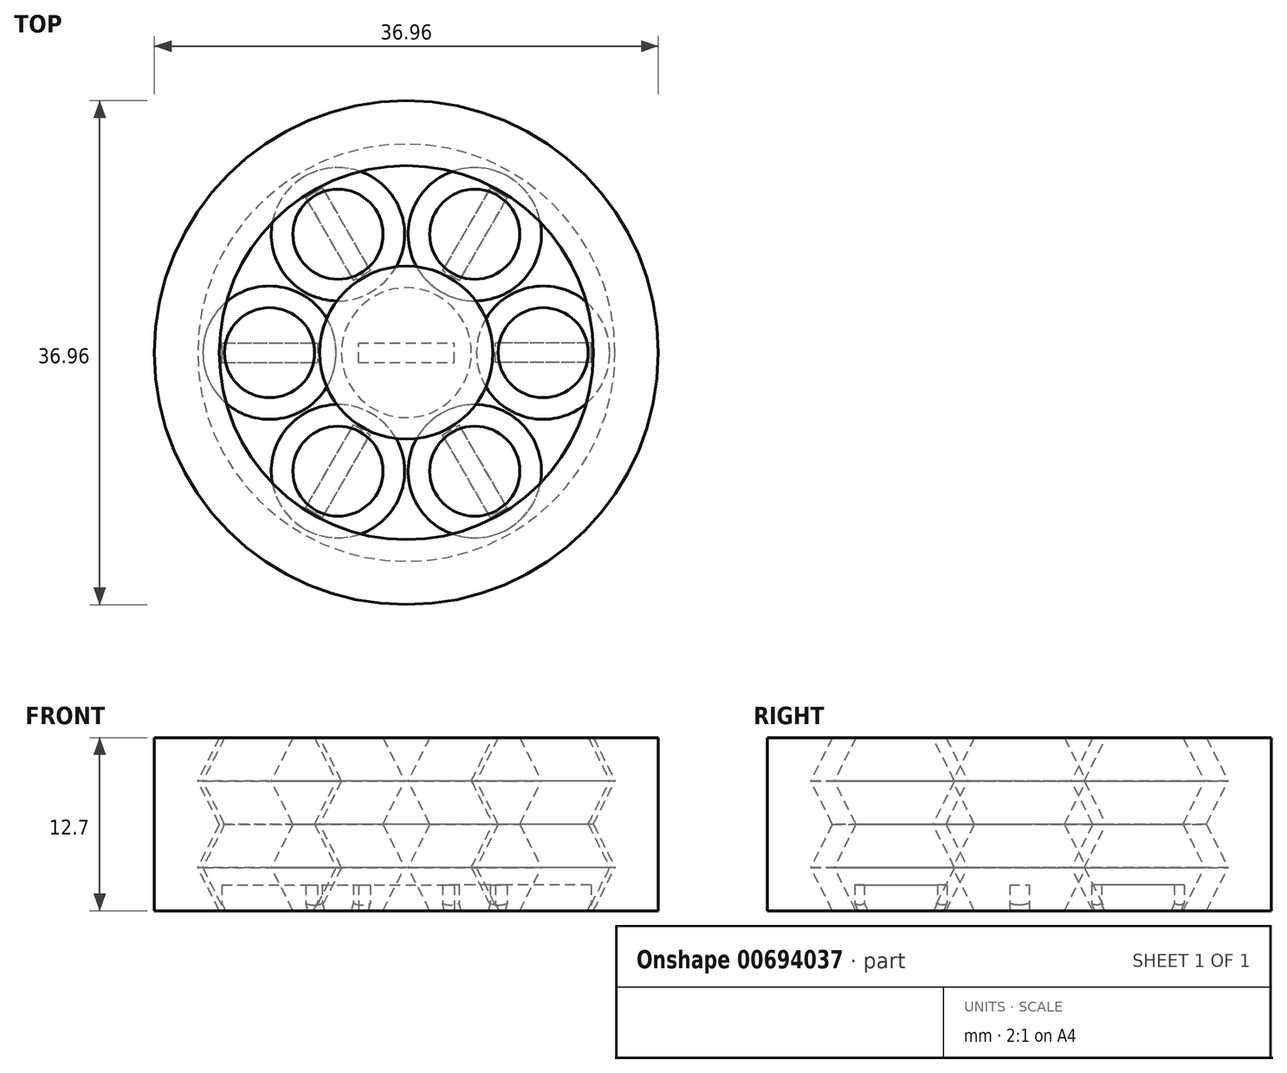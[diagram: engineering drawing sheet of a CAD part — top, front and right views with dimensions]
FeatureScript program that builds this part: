
annotation { "Feature Type Name" : "Feature", "Feature Type Description" : "" }
export const myFeature = defineFeature(function(context is Context, id is Id, definition is map)
    precondition{}
    {
        {
            var Q0;
            Q0=qCreatedBy(makeId("Front.planeOp"),FACE);
            var sketch = newSketch(context, id + "F0", { "sketchPlane" : qUnion([Q0])});
            skLineSegment(sketch, "E0", {"start": v(0, 0) * mm, "end": v(3.17, 0) * mm});
            skLineSegment(sketch, "E1", {"start": v(3.17, 12.7) * mm, "end": v(0, 12.7) * mm});
            skLineSegment(sketch, "E2", {"start": v(6.35, 0) * mm, "end": v(6.86, 0) * mm});
            skLineSegment(sketch, "E3", {"start": v(6.86, 12.7) * mm, "end": v(10.03, 12.7) * mm});
            skLineSegment(sketch, "E4", {"start": v(8.45, 12.7) * mm, "end": v(8.45, 0) * mm});
            skLineSegment(sketch, "E5", {"start": v(8.45, 0) * mm, "end": v(6.86, 0) * mm});
            skLineSegment(sketch, "E6.MirrorCS", {"start": v(12.38, 3.68) * mm, "end": v(12.54, 3.68) * mm});
            skLineSegment(sketch, "E7.MirrorCS", {"start": v(8.45, 0) * mm, "end": v(10.03, 0) * mm});
            skLineSegment(sketch, "E8.MirrorCS", {"start": v(16.9, 0) * mm, "end": v(13.72, 0) * mm});
            skLineSegment(sketch, "E9.MirrorCS", {"start": v(13.72, 12.7) * mm, "end": v(16.9, 12.7) * mm});
            skLineSegment(sketch, "E10.MirrorCS", {"start": v(16.9, 12.7) * mm, "end": v(16.9, 0) * mm});
            skPoint(sketch, "E11.orphan", {"position": v(6.35, 3.18) * mm});
            skPoint(sketch, "E12.start.orphan", {"position": v(6.35, 9.53) * mm});
            skPoint(sketch, "E13.orphan", {"position": v(6.35, 12.7) * mm});
            skPoint(sketch, "E14.orphan", {"position": v(10.54, 9.53) * mm});
            skPoint(sketch, "E15.MirrorCS.end.orphan", {"position": v(10.54, 12.7) * mm});
            skPoint(sketch, "E16.orphan", {"position": v(10.54, 0) * mm});
            skPoint(sketch, "E17.orphan", {"position": v(10.54, 3.18) * mm});
            skLineSegment(sketch, "E18", {"start": v(5.27, 0) * mm, "end": v(6.86, 0) * mm});
            skLineSegment(sketch, "E19", {"start": v(12.13, 0) * mm, "end": v(11.62, 0) * mm});
            skLineSegment(sketch, "E20", {"start": v(10.03, 0) * mm, "end": v(11.62, 0) * mm});
            skPoint(sketch, "E21.orphan", {"position": v(6.86, 3.68) * mm});
            skPoint(sketch, "E22.orphan", {"position": v(10.03, 3.68) * mm});
            skLineSegment(sketch, "E23", {"start": v(5.27, 12.7) * mm, "end": v(6.86, 12.7) * mm});
            skLineSegment(sketch, "E24", {"start": v(11.62, 12.7) * mm, "end": v(10.03, 12.7) * mm});
            skPoint(sketch, "E25.orphan", {"position": v(6.86, 9.02) * mm});
            skPoint(sketch, "E26.MirrorCS.end.orphan", {"position": v(10.03, 12.7) * mm});
            skPoint(sketch, "E26.MirrorCS.start.orphan", {"position": v(10.03, 9.02) * mm});
            skPoint(sketch, "E27.MirrorCS.start.orphan", {"position": v(13.72, 9.53) * mm});
            skPoint(sketch, "E28.MirrorCS.start.orphan", {"position": v(13.2, 3.68) * mm});
            skPoint(sketch, "E29.MirrorCS.end.orphan", {"position": v(13.72, 3.18) * mm});
            skLineSegment(sketch, "E30.trimOffspring", {"start": v(13.05, 3.68) * mm, "end": v(13.2, 3.68) * mm});
            skPoint(sketch, "E31.end.orphan", {"position": v(11.62, 3.68) * mm});
            skPoint(sketch, "E32.end.orphan", {"position": v(3.18, 9.53) * mm});
            skPoint(sketch, "E33.end.orphan", {"position": v(5.27, 9.02) * mm});
            skPoint(sketch, "E34.end.orphan", {"position": v(5.27, 3.68) * mm});
            skPoint(sketch, "E35.trimOffspring.end.orphan", {"position": v(3.18, 3.18) * mm});
            skPoint(sketch, "E36.orphan", {"position": v(13.72, 6.35) * mm});
            skLineSegment(sketch, "E37", {"start": v(3.68, 3.18) * mm, "end": v(5.27, 0) * mm});
            skLineSegment(sketch, "E38", {"start": v(3.68, 3.18) * mm, "end": v(5.27, 6.35) * mm});
            skLineSegment(sketch, "E39", {"start": v(5.27, 6.35) * mm, "end": v(3.68, 9.53) * mm});
            skLineSegment(sketch, "E40", {"start": v(5.27, 12.7) * mm, "end": v(3.68, 9.53) * mm});
            skLineSegment(sketch, "E41", {"start": v(4.76, 12.7) * mm, "end": v(3.18, 9.53) * mm});
            skLineSegment(sketch, "E42", {"start": v(4.76, 6.35) * mm, "end": v(3.18, 9.53) * mm});
            skLineSegment(sketch, "E43", {"start": v(4.76, 6.35) * mm, "end": v(3.18, 3.18) * mm});
            skLineSegment(sketch, "E44", {"start": v(4.76, 0) * mm, "end": v(3.18, 3.18) * mm});
            skLineSegment(sketch, "E45", {"start": v(4.76, 0) * mm, "end": v(3.17, 0) * mm});
            skLineSegment(sketch, "E46", {"start": v(4.76, 12.7) * mm, "end": v(3.17, 12.7) * mm});
            skPoint(sketch, "E47.orphan", {"position": v(3.17, 6.35) * mm});
            skLineSegment(sketch, "E48.MirrorCS", {"start": v(12.13, 0) * mm, "end": v(13.72, 3.17) * mm});
            skLineSegment(sketch, "E49.MirrorCS", {"start": v(12.13, 0) * mm, "end": v(13.72, 0) * mm});
            skLineSegment(sketch, "E50.MirrorCS", {"start": v(12.13, 6.35) * mm, "end": v(13.72, 3.18) * mm});
            skLineSegment(sketch, "E51.MirrorCS", {"start": v(12.13, 6.35) * mm, "end": v(13.72, 9.53) * mm});
            skLineSegment(sketch, "E52.MirrorCS", {"start": v(12.13, 12.7) * mm, "end": v(13.72, 9.53) * mm});
            skLineSegment(sketch, "E53.MirrorCS", {"start": v(12.13, 12.7) * mm, "end": v(13.72, 12.7) * mm});
            skLineSegment(sketch, "E54", {"start": v(0, 12.7) * mm, "end": v(-1.59, 12.7) * mm});
            skLineSegment(sketch, "E55", {"start": v(-1.59, 0) * mm, "end": v(0, 0) * mm});
            skLineSegment(sketch, "E56", {"start": v(-1.59, 12.7) * mm, "end": v(-1.59, 0) * mm});
            skPoint(sketch, "E57.start.orphan", {"position": v(-3.18, 12.7) * mm});
            skPoint(sketch, "E58.orphan", {"position": v(-3.18, 0) * mm});
            skLineSegment(sketch, "E59", {"start": v(11.62, 12.7) * mm, "end": v(11.75, 12.7) * mm});
            skLineSegment(sketch, "E60", {"start": v(11.75, 12.7) * mm, "end": v(13.34, 9.53) * mm});
            skLineSegment(sketch, "E61", {"start": v(13.34, 9.53) * mm, "end": v(11.75, 6.35) * mm});
            skLineSegment(sketch, "E62", {"start": v(11.75, 6.35) * mm, "end": v(13.34, 3.18) * mm});
            skLineSegment(sketch, "E63", {"start": v(13.34, 3.18) * mm, "end": v(11.75, 0) * mm});
            skSolve(sketch);
        }
        {
            var Q0;
            {var subQ0=sQuery(id+"F0.wireOp",EDGE,"E4");Q0=makeQuery(id+"F0.imprint","IMPRINT",FACE,{"disambiguationData":[TD([[makeQuery(id+"F0.imprint","IMPRINT",EDGE,{"derivedFrom":subQ0}),1.0]])]});}
            var Q1;
            Q1=sQuery(id+"F0.wireOp",EDGE,"E4");
            revolve(context, id + "F1", {"entities" : qUnion([Q0]), "axis" : qUnion([Q1]), "revolveType" : RevolveType.FULL});
        }
        {
            var Q0;
            Q0=makeQuery(id+"F0.imprint","IMPRINT",FACE,{"disambiguationData":[TD([[makeQuery(id+"F0.imprint","IMPRINT",EDGE,{"derivedFrom":sQuery(id+"F0.wireOp",EDGE,"6038c564-a6ce-4f6b-803a-afe6331ad0240.MirrorCS")}),-1.0]])]});
            var Q1;
            Q1=makeQuery(id+"F0.imprint","IMPRINT",FACE,{"disambiguationData":[TD([[makeQuery(id+"F0.imprint","IMPRINT",EDGE,{"derivedFrom":sQuery(id+"F0.wireOp",EDGE,"E0")}),1.0]])]});
            var Q2;
            Q2=makeQuery(id+"F0.imprint","IMPRINT",FACE,{"disambiguationData":[TD([[makeQuery(id+"F0.imprint","IMPRINT",EDGE,{"derivedFrom":sQuery(id+"F0.wireOp",EDGE,"E8.MirrorCS")}),-1.0]])]});
            var Q3;
            Q3=sQuery(id+"F0.wireOp",EDGE,"E56");
            revolve(context, id + "F2", {"entities" : qUnion([Q0, Q1, Q2]), "axis" : qUnion([Q3]), "revolveType" : RevolveType.FULL});
        }
        {
            var Q0;
            Q0=makeQuery(id+"F2.opRevolve","SWEPT_FACE",FACE,{"disambiguationData":[OSD([sQuery(id+"F0.wireOp",EDGE,"E0")])]});
            var sketch = newSketch(context, id + "F3", { "sketchPlane" : qUnion([Q0])});
            skPoint(sketch, "E64.middle", {"position": v(0, 0) * mm});
            skLineSegment(sketch, "E65.bottom", {"start": v(-5.1, 0.71) * mm, "end": v(1.92, 0.71) * mm});
            skLineSegment(sketch, "E65.top", {"start": v(-5.1, -0.71) * mm, "end": v(1.92, -0.71) * mm});
            skLineSegment(sketch, "E65.left", {"start": v(-5.1, 0.71) * mm, "end": v(-5.1, -0.71) * mm});
            skLineSegment(sketch, "E65.right", {"start": v(1.92, 0.71) * mm, "end": v(1.92, -0.71) * mm});
            skPoint(sketch, "E65.middle", {"position": v(-1.59, 0) * mm});
            skSolve(sketch);
        }
        {
            var Q0;
            Q0=makeQuery(id+"F3.imprint","IMPRINT",FACE,{"disambiguationData":[TD([[makeQuery(id+"F3.imprint","IMPRINT",EDGE,{"derivedFrom":sQuery(id+"F3.wireOp",EDGE,"E65.bottom")}),-1.0]])]});
            extrude(context, id + "F4", {"entities" : qUnion([Q0]), "operationType" : NewBodyOperationType.REMOVE, "oppositeDirection" : true, "depth" : 1.9 * mm, "offsetDistance" : 25.4 * mm});
        }
        {
            var Q0;
            Q0=makeQuery(id+"F1.opRevolve","SWEPT_FACE",FACE,{"disambiguationData":[OSD([sQuery(id+"F0.wireOp",EDGE,"E7.MirrorCS"),sQuery(id+"F0.wireOp",EDGE,"E19"),sQuery(id+"F0.wireOp",EDGE,"E20")])]});
            var sketch = newSketch(context, id + "F5", { "sketchPlane" : qUnion([Q0])});
            skLineSegment(sketch, "E66.bottom", {"start": v(11.95, 0.71) * mm, "end": v(4.94, 0.71) * mm});
            skLineSegment(sketch, "E66.top", {"start": v(11.95, -0.71) * mm, "end": v(4.94, -0.71) * mm});
            skLineSegment(sketch, "E66.left", {"start": v(11.95, 0.71) * mm, "end": v(11.95, -0.71) * mm});
            skLineSegment(sketch, "E66.right", {"start": v(4.94, 0.71) * mm, "end": v(4.94, -0.71) * mm});
            skPoint(sketch, "E66.middle", {"position": v(8.45, 0) * mm});
            skSolve(sketch);
        }
        {
            var Q0;
            Q0 = qSketchRegion(id + "F5", true);
            extrude(context, id + "F6", {"entities" : qUnion([Q0]), "operationType" : NewBodyOperationType.REMOVE, "oppositeDirection" : true, "depth" : 1.9 * mm, "offsetDistance" : 25.4 * mm});
        }
        {
            var Q0;
            Q0=makeQuery(id+"F1.opRevolve","SWEPT_BODY",BODY,{"disambiguationData":[OSD([sQuery(id+"F0.wireOp",EDGE,"E3"),sQuery(id+"F0.wireOp",EDGE,"E4"),sQuery(id+"F0.wireOp",EDGE,"E7.MirrorCS"),sQuery(id+"F0.wireOp",EDGE,"E19"),sQuery(id+"F0.wireOp",EDGE,"E20"),sQuery(id+"F0.wireOp",EDGE,"E24"),sQuery(id+"F0.wireOp",EDGE,"E59"),sQuery(id+"F0.wireOp",EDGE,"E60"),sQuery(id+"F0.wireOp",EDGE,"E61"),sQuery(id+"F0.wireOp",EDGE,"E62"),sQuery(id+"F0.wireOp",EDGE,"E63")])]});
            var Q1;
            Q1=sQuery(id+"F0.wireOp",EDGE,"E56");
            circularPattern(context, id + "F7", {"entities" : qUnion([Q0]), "axis" : qUnion([Q1]), "angle" : 360 * degree, "instanceCount" : 6, "equalSpace" : true});
        }
    });
